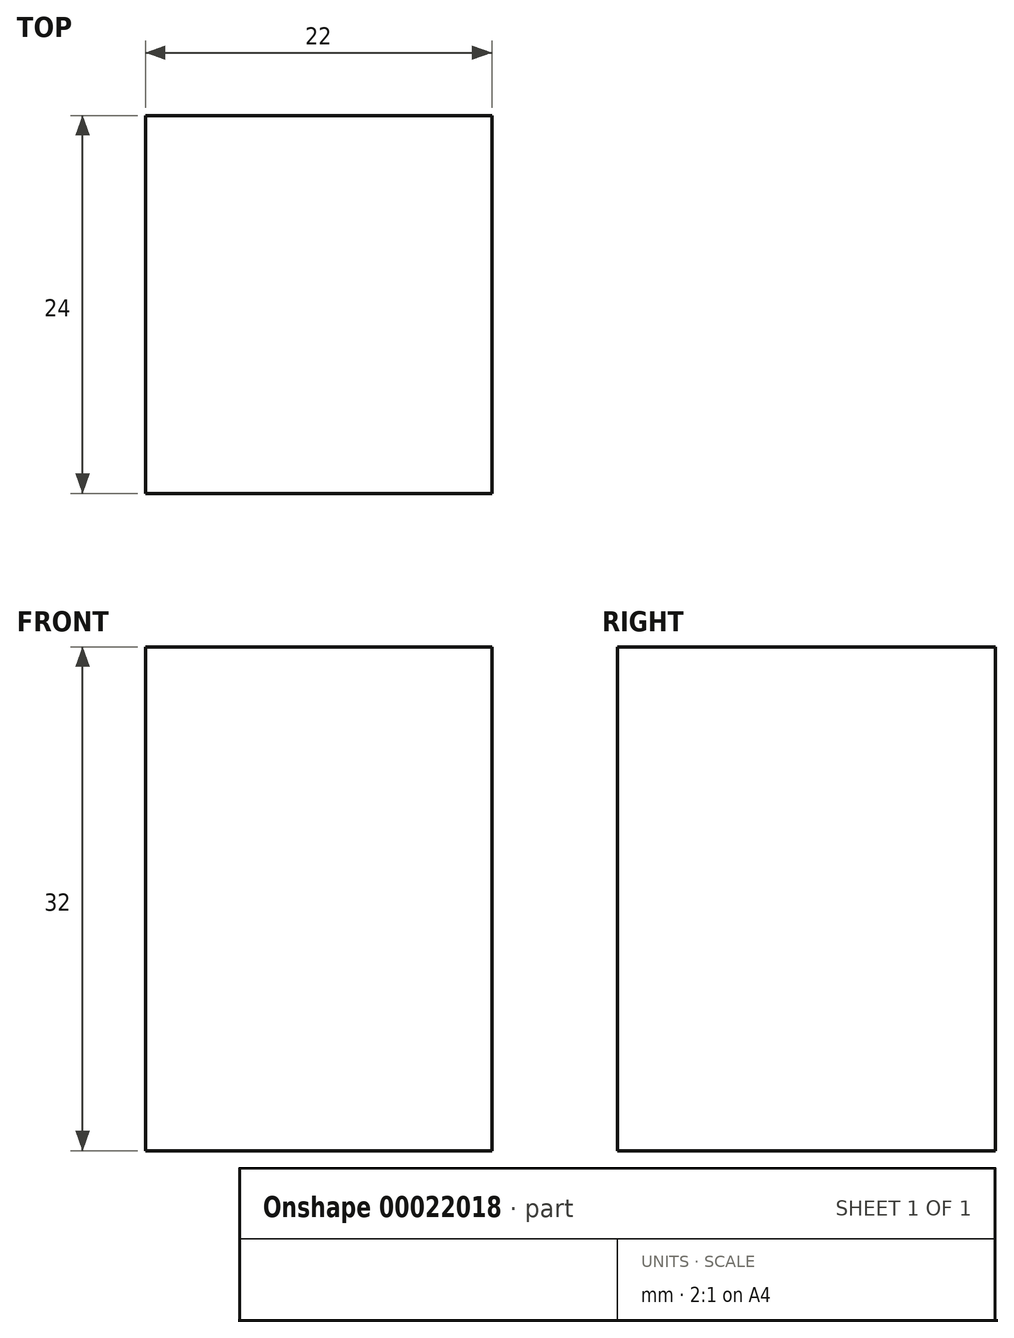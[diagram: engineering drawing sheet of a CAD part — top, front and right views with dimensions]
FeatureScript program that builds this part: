
annotation { "Feature Type Name" : "Feature", "Feature Type Description" : "" }
export const myFeature = defineFeature(function(context is Context, id is Id, definition is map)
    precondition{}
    {
        {
            var Q0;
            Q0=qCreatedBy(makeId("Top.planeOp"),FACE);
            var sketch = newSketch(context, id + "F0", { "sketchPlane" : qUnion([Q0])});
            skLineSegment(sketch, "E0.bottom", {"start": v(-22, 15.28) * mm, "end": v(0, 15.28) * mm});
            skLineSegment(sketch, "E0.top", {"start": v(-22, -8.72) * mm, "end": v(0, -8.72) * mm});
            skLineSegment(sketch, "E0.left", {"start": v(-22, 15.28) * mm, "end": v(-22, -8.72) * mm});
            skLineSegment(sketch, "E0.right", {"start": v(0, 15.28) * mm, "end": v(0, -8.72) * mm});
            skSolve(sketch);
        }
        {
            var Q0;
            Q0 = qSketchRegion(id + "F0", true);
            extrude(context, id + "F1", {"entities" : qUnion([Q0]), "depth" : 32 * mm});
        }
    });
